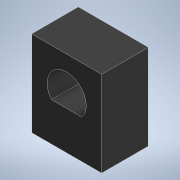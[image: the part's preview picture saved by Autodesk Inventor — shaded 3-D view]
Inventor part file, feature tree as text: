
AUTODESK INVENTOR PART (.ipt)
format: ipt  version: 2021 (Build 250183000, 183)  size: 120,832 bytes
history: native  units: mm
features: extrude x2, sketch x2
ambient origin geometry x8: Origin, YZ Plane, XZ Plane, XY Plane, X Axis, Y Axis, Z Axis, Center Point
bodies: Solid1 (feature_tree)
feature tree (4):
  extrude  "Extrusion1"  Depth=18.0mm
  extrude  "Extrusion2"  Depth=8.0mm
  sketch  "Sketch1"  dims[d1=10.0mm d2=18.0mm]
  sketch  "Sketch2"  dims[d3=9.0mm d4=13.0mm d5=12.0mm d6=0.0mm d7=2.8mm d8=3.0mm d9=3.0mm d10=8.0mm d11=0.0mm d18=3.1mm]
